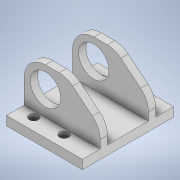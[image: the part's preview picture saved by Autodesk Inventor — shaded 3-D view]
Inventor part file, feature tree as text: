
AUTODESK INVENTOR PART (.ipt)
format: ipt  version: 2022 (Build 260153000, 153)  size: 185,344 bytes
history: native  units: mm
features: extrude x3, sketch x3, projected_geometry x2, fillet x1
ambient origin geometry x8: Origin, YZ Plane, XZ Plane, XY Plane, X Axis, Y Axis, Z Axis, Center Point
bodies: Solid1 (feature_tree)
feature tree (9):
  extrude  "Extrusion1"  Depth=25.0mm
  extrude  "Extrusion2"  Depth=10.0mm
  extrude  "Extrusion3"  Depth=7.0mm
  fillet  "Fillet1"  Radius=25.5mm
  sketch  "Sketch1"  dims[d0=30.0mm d1=25.0mm]
  sketch  "Sketch2"  dims[d2=3.0mm d3=20.0mm d5=22.0mm d6=20.0mm d8=10.0mm]
  projected_geometry  "Projected Loop1"
  sketch  "Sketch3"  dims[d11=20.0mm d12=4.0mm d13=25.5mm d14=0.0mm d15=3.0mm d16=3.0mm d17=3.0mm d19=13.5mm d20=2.4mm d21=2.4mm d22=5.85mm d23=25.5mm d24=0.0mm d25=8.0mm d26=7.0mm d27=7.0mm d28=14.0mm d29=6.0mm d30=10.0mm d31=25.5mm d32=0.0mm d33=7.0mm]
  projected_geometry  "Projected Loop2"
